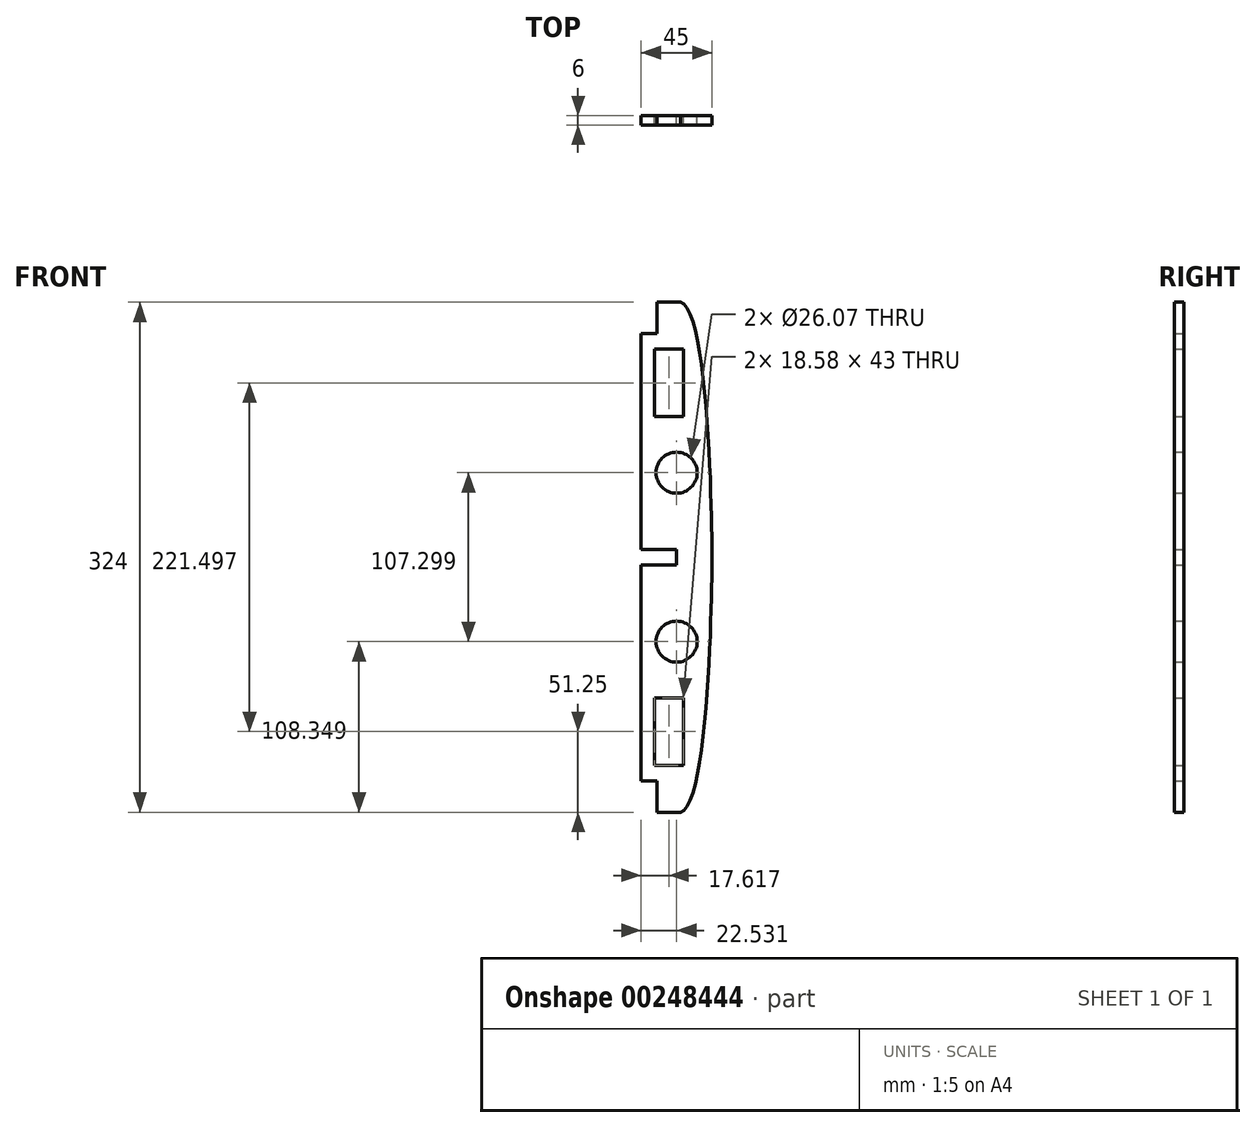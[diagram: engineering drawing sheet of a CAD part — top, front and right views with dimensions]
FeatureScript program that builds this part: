
annotation { "Feature Type Name" : "Feature", "Feature Type Description" : "" }
export const myFeature = defineFeature(function(context is Context, id is Id, definition is map)
    precondition{}
    {
        {
            var Q0;
            Q0=qCreatedBy(makeId("Front.planeOp"),FACE);
            var sketch = newSketch(context, id + "F0", { "sketchPlane" : qUnion([Q0])});
            skLineSegment(sketch, "E0.bottom", {"start": v(469.38, 222.22) * mm, "end": v(434.38, 222.22) * mm});
            skLineSegment(sketch, "E0.top", {"start": v(469.38, 60.22) * mm, "end": v(424.38, 60.22) * mm});
            skLineSegment(sketch, "E0.left", {"start": v(469.38, 222.22) * mm, "end": v(469.38, 60.22) * mm});
            skFitSpline(sketch, "E1", {"points": [v(449.38, 222.22) * mm, v(469.38, 60.22) * mm], "startDerivative": vector(60, -14.58) * mm, "endDerivative": vector(-0.42, 27.38) * mm});
            skLineSegment(sketch, "E2.bottom", {"start": v(451.29, 192.47) * mm, "end": v(432.7, 192.47) * mm});
            skLineSegment(sketch, "E2.top", {"start": v(451.29, 149.46) * mm, "end": v(432.7, 149.46) * mm});
            skLineSegment(sketch, "E2.left", {"start": v(451.29, 192.47) * mm, "end": v(451.29, 149.46) * mm});
            skLineSegment(sketch, "E2.right", {"start": v(432.7, 192.47) * mm, "end": v(432.7, 149.46) * mm});
            skCircle(sketch, "E3", {"center": v(446.91, 113.87) * mm, "radius": 13.03 * mm});
            skLineSegment(sketch, "E4.MirrorCS", {"start": v(451.29, -72.03) * mm, "end": v(451.29, -29.03) * mm});
            skLineSegment(sketch, "E5.MirrorCS", {"start": v(469.38, -101.78) * mm, "end": v(434.38, -101.78) * mm});
            skLineSegment(sketch, "E6.MirrorCS", {"start": v(469.38, -101.78) * mm, "end": v(469.38, 60.22) * mm});
            skFitSpline(sketch, "E7.MirrorCS", {"points": [v(449.38, -101.78) * mm, v(469.38, 60.22) * mm], "startDerivative": vector(60, 14.58) * mm, "endDerivative": vector(-0.42, -27.38) * mm});
            skLineSegment(sketch, "E8.MirrorCS", {"start": v(432.7, -72.03) * mm, "end": v(432.7, -29.03) * mm});
            skLineSegment(sketch, "E9.MirrorCS", {"start": v(451.29, -72.03) * mm, "end": v(432.7, -72.03) * mm});
            skLineSegment(sketch, "E10.MirrorCS", {"start": v(451.29, -29.03) * mm, "end": v(432.7, -29.03) * mm});
            skCircle(sketch, "E11.MirrorC", {"center": v(446.91, 6.57) * mm, "radius": 13.03 * mm});
            skLineSegment(sketch, "E12", {"start": v(446.88, 60.22) * mm, "end": v(446.88, 55.22) * mm});
            skLineSegment(sketch, "E13", {"start": v(446.88, 60.22) * mm, "end": v(446.88, 65.22) * mm});
            skLineSegment(sketch, "E14", {"start": v(446.88, 65.22) * mm, "end": v(424.38, 65.22) * mm});
            skLineSegment(sketch, "E15", {"start": v(446.88, 55.22) * mm, "end": v(424.38, 55.22) * mm});
            skLineSegment(sketch, "E16", {"start": v(434.38, 222.22) * mm, "end": v(434.38, 202.22) * mm});
            skLineSegment(sketch, "E17", {"start": v(434.38, 202.22) * mm, "end": v(424.38, 202.22) * mm});
            skLineSegment(sketch, "E18", {"start": v(424.38, 202.22) * mm, "end": v(424.38, 60.22) * mm});
            skLineSegment(sketch, "E19.MirrorCS", {"start": v(434.38, -101.78) * mm, "end": v(434.38, -81.78) * mm});
            skLineSegment(sketch, "E20.MirrorCS", {"start": v(434.38, -81.78) * mm, "end": v(424.38, -81.78) * mm});
            skLineSegment(sketch, "E21", {"start": v(424.38, -81.78) * mm, "end": v(424.38, 60.22) * mm});
            skSolve(sketch);
        }
        {
            var Q0;
            Q0=makeQuery(id+"F0.imprint","IMPRINT",FACE,{"disambiguationData":[TD([[makeQuery(id+"F0.imprint","IMPRINT",EDGE,{"derivedFrom":sQuery(id+"F0.wireOp",EDGE,"E4.MirrorCS")}),-1.0]])]});
            var Q1;
            Q1=makeQuery(id+"F0.imprint","IMPRINT",FACE,{"disambiguationData":[TD([[makeQuery(id+"F0.imprint","IMPRINT",EDGE,{"derivedFrom":sQuery(id+"F0.wireOp",EDGE,"E2.bottom")}),-1.0]])]});
            extrude(context, id + "F1", {"entities" : qUnion([Q0, Q1]), "depth" : 6 * mm});
        }
    });
